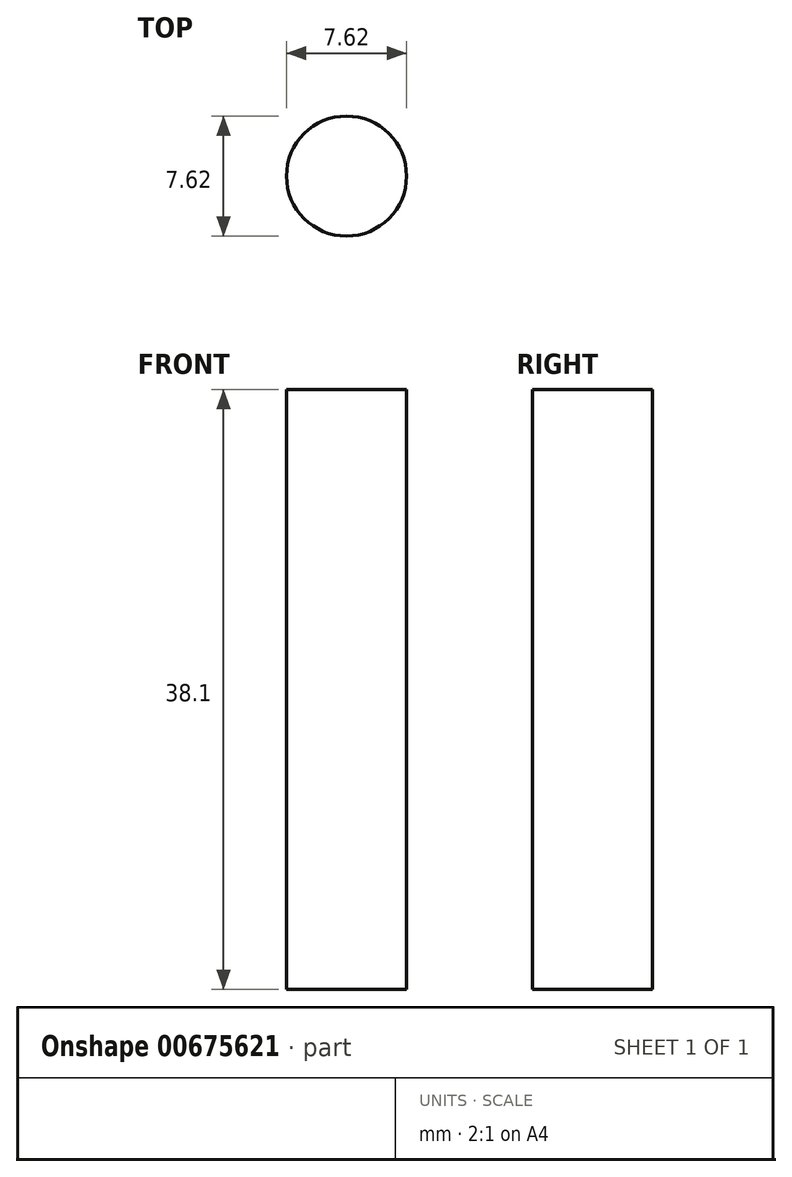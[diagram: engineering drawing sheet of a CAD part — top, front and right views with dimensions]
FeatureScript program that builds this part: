
annotation { "Feature Type Name" : "Feature", "Feature Type Description" : "" }
export const myFeature = defineFeature(function(context is Context, id is Id, definition is map)
    precondition{}
    {
        {
            var Q0;
            Q0=qCreatedBy(makeId("Front.planeOp"),FACE);
            var sketch = newSketch(context, id + "F0", { "sketchPlane" : qUnion([Q0])});
            skLineSegment(sketch, "E0", {"start": v(0, 0) * mm, "end": v(-3.81, 0) * mm});
            skLineSegment(sketch, "E1", {"start": v(-3.81, 0) * mm, "end": v(-3.81, 38.1) * mm});
            skLineSegment(sketch, "E2", {"start": v(-3.81, 38.1) * mm, "end": v(0, 38.1) * mm});
            skLineSegment(sketch, "E3", {"start": v(0, 38.1) * mm, "end": v(0, 0) * mm});
            skSolve(sketch);
        }
        {
            var Q0;
            Q0 = qSketchRegion(id + "F0", true);
            var Q1;
            Q1=sQuery(id+"F0.wireOp",EDGE,"E3");
            revolve(context, id + "F1", {"entities" : qUnion([Q0]), "axis" : qUnion([Q1]), "revolveType" : RevolveType.FULL});
        }
    });
